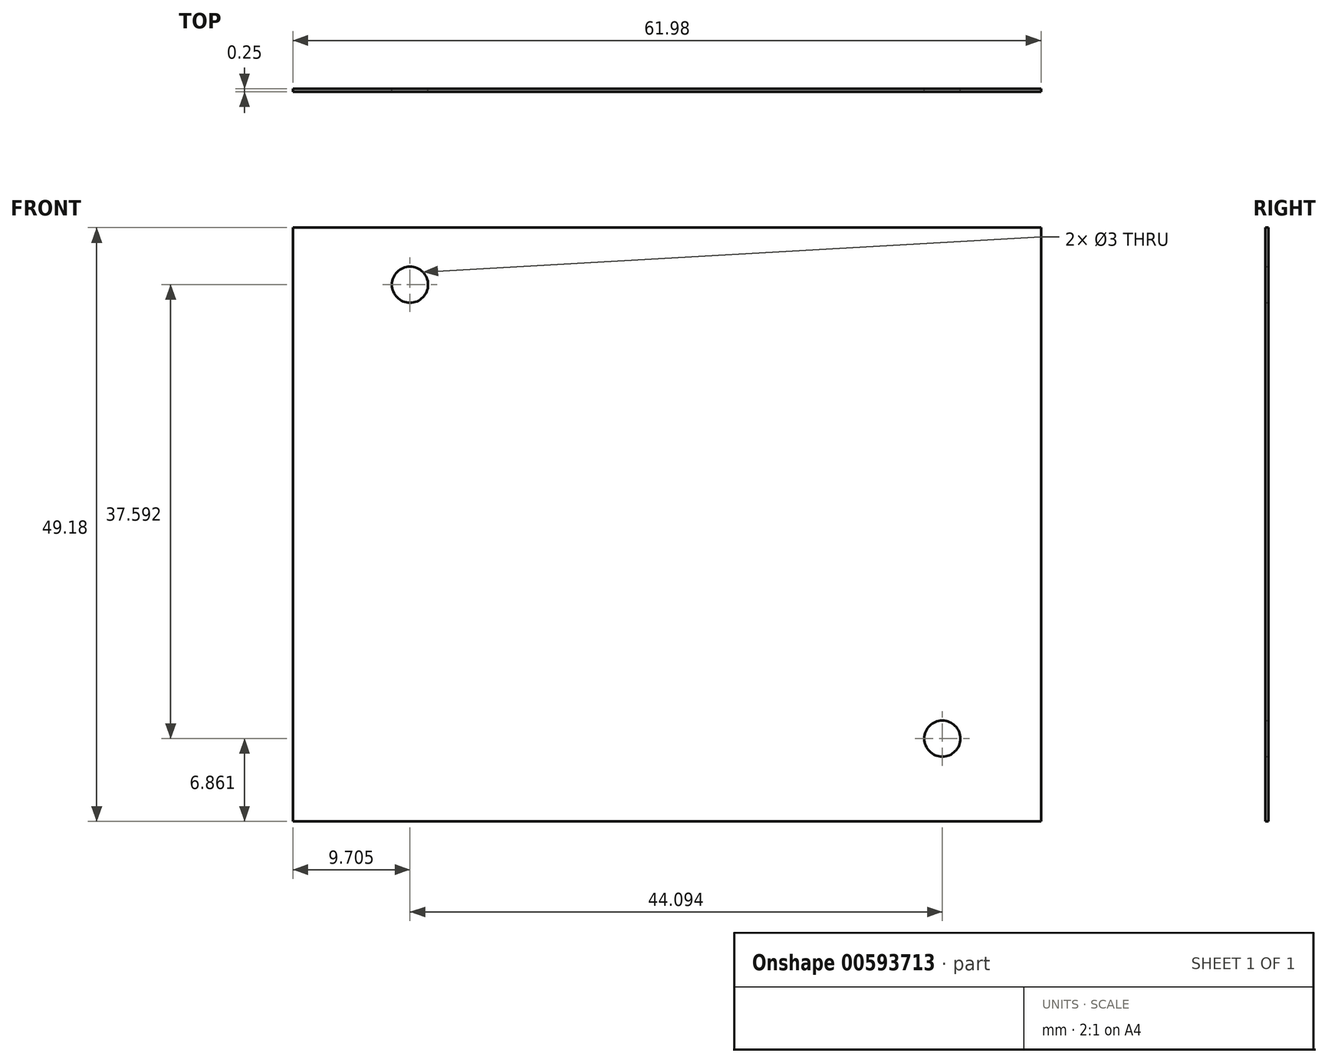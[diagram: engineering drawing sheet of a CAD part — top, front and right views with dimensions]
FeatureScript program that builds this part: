
annotation { "Feature Type Name" : "Feature", "Feature Type Description" : "" }
export const myFeature = defineFeature(function(context is Context, id is Id, definition is map)
    precondition{}
    {
        {
            var Q0;
            Q0=qCreatedBy(makeId("Front.planeOp"),FACE);
            var sketch = newSketch(context, id + "F0", { "sketchPlane" : qUnion([Q0])});
            skLineSegment(sketch, "E0.bottom", {"start": v(-30.99, -24.59) * mm, "end": v(30.99, -24.59) * mm});
            skLineSegment(sketch, "E0.top", {"start": v(-30.99, 24.59) * mm, "end": v(30.99, 24.59) * mm});
            skLineSegment(sketch, "E0.left", {"start": v(-30.99, -24.59) * mm, "end": v(-30.99, 24.59) * mm});
            skLineSegment(sketch, "E0.right", {"start": v(30.99, -24.59) * mm, "end": v(30.99, 24.59) * mm});
            skCircle(sketch, "E1", {"center": v(-21.29, 19.86) * mm, "radius": 1.5 * mm});
            skCircle(sketch, "E2", {"center": v(22.8, -17.73) * mm, "radius": 1.5 * mm});
            skPoint(sketch, "E3.endSnap0", {"position": v(0, -24.59) * mm});
            skSolve(sketch);
        }
        {
            var Q0;
            Q0=makeQuery(id+"F0.imprint","IMPRINT",FACE,{"disambiguationData":[TD([[makeQuery(id+"F0.imprint","IMPRINT",EDGE,{"derivedFrom":sQuery(id+"F0.wireOp",EDGE,"E0.bottom")}),1.0]])]});
            extrude(context, id + "F1", {"entities" : qUnion([Q0]), "depth" : 0.25 * mm, "offsetDistance" : 25.4 * mm});
        }
    });
